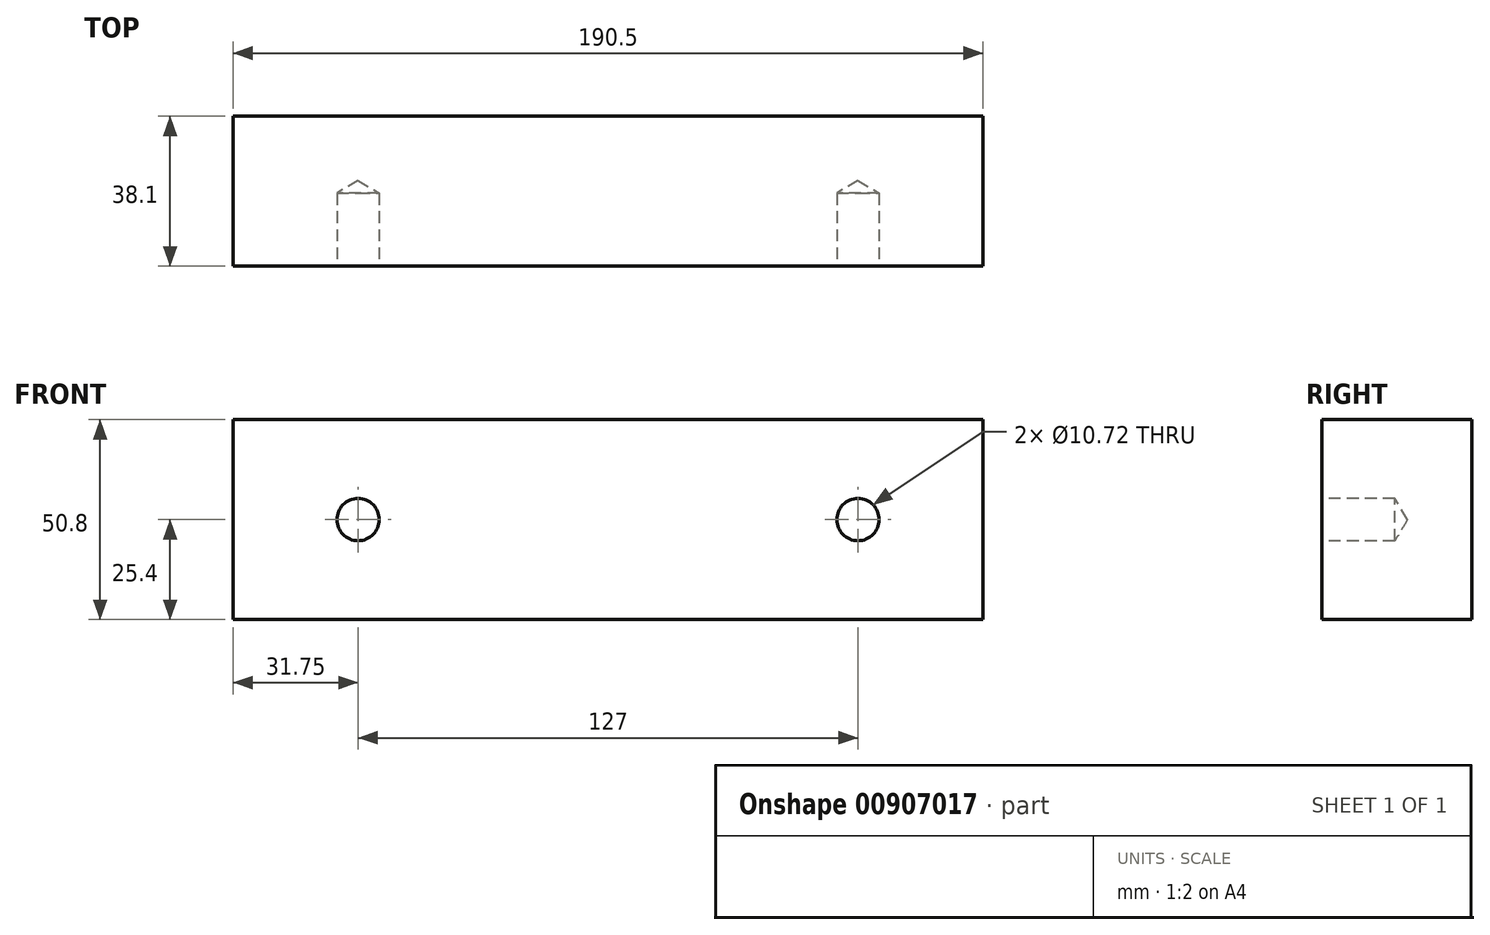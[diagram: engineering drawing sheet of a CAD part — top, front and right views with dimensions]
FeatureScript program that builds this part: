
annotation { "Feature Type Name" : "Feature", "Feature Type Description" : "" }
export const myFeature = defineFeature(function(context is Context, id is Id, definition is map)
    precondition{}
    {
        {
            var Q0;
            Q0=qCreatedBy(makeId("Front.planeOp"),FACE);
            var sketch = newSketch(context, id + "F0", { "sketchPlane" : qUnion([Q0])});
            skLineSegment(sketch, "E0.bottom", {"start": v(95.25, 25.4) * mm, "end": v(-95.25, 25.4) * mm});
            skLineSegment(sketch, "E0.top", {"start": v(95.25, -25.4) * mm, "end": v(-95.25, -25.4) * mm});
            skLineSegment(sketch, "E0.left", {"start": v(95.25, 25.4) * mm, "end": v(95.25, -25.4) * mm});
            skLineSegment(sketch, "E0.right", {"start": v(-95.25, 25.4) * mm, "end": v(-95.25, -25.4) * mm});
            skPoint(sketch, "E0.middle", {"position": v(0, 0) * mm});
            skSolve(sketch);
        }
        {
            var Q0;
            Q0=makeQuery(id+"F0.imprint","IMPRINT",FACE,{"disambiguationData":[TD([[makeQuery(id+"F0.imprint","IMPRINT",EDGE,{"derivedFrom":sQuery(id+"F0.wireOp",EDGE,"E0.bottom")}),1.0]])]});
            extrude(context, id + "F1", {"entities" : qUnion([Q0]), "depth" : 38.1 * mm, "offsetDistance" : 25.4 * mm});
        }
        {
            var Q0;
            Q0=makeQuery(id+"F1.opExtrude","CAP_FACE",FACE,{"disambiguationData":[OSD([sQuery(id+"F0.wireOp",EDGE,"E0.bottom"),sQuery(id+"F0.wireOp",EDGE,"E0.top"),sQuery(id+"F0.wireOp",EDGE,"E0.left"),sQuery(id+"F0.wireOp",EDGE,"E0.right")])],"isStart":false});
            var sketch = newSketch(context, id + "F2", { "sketchPlane" : qUnion([Q0])});
            skLineSegment(sketch, "E1", {"start": v(-63.5, 0) * mm, "end": v(63.5, 0) * mm, "construction": true});
            skSolve(sketch);
        }
        {
            var Q0;
            Q0=sQuery(id+"F2.wireOp",VERTEX,"E1.start");
            var Q1;
            Q1=sQuery(id+"F2.wireOp",VERTEX,"E1.end");
            var Q2;
            Q2=makeQuery(id+"F1.opExtrude","SWEPT_BODY",BODY,{"disambiguationData":[OSD([sQuery(id+"F0.wireOp",EDGE,"E0.bottom"),sQuery(id+"F0.wireOp",EDGE,"E0.top"),sQuery(id+"F0.wireOp",EDGE,"E0.left"),sQuery(id+"F0.wireOp",EDGE,"E0.right")])]});
            hole(context, id + "F3", {"style" : HoleStyle.SIMPLE, "endStyle" : HoleEndStyle.BLIND, "standardTappedOrClearance" : lookupTablePath({ "standard" : "ANSI", "engagement" : "75%", "pitch" : "13 tpi", "size" : "1/2", "type" : "Tapped" }), "standardBlindInLast" : lookupTablePath({ "fit" : "Free", "standard" : "ANSI", "engagement" : "75%", "pitch" : "13 tpi", "size" : "1/2", "type" : "Clearance & tapped" }), "holeDiameter" : 10.72 * mm, "majorDiameter" : 12.7 * mm, "showTappedDepth" : true, "holeDepth" : 18.56 * mm, "isTappedThrough" : true, "tappedDepth" : 12.7 * mm, "tapClearance" : 3, "locations" : qUnion([Q0, Q1]), "scope" : qUnion([Q2])});
        }
    });
